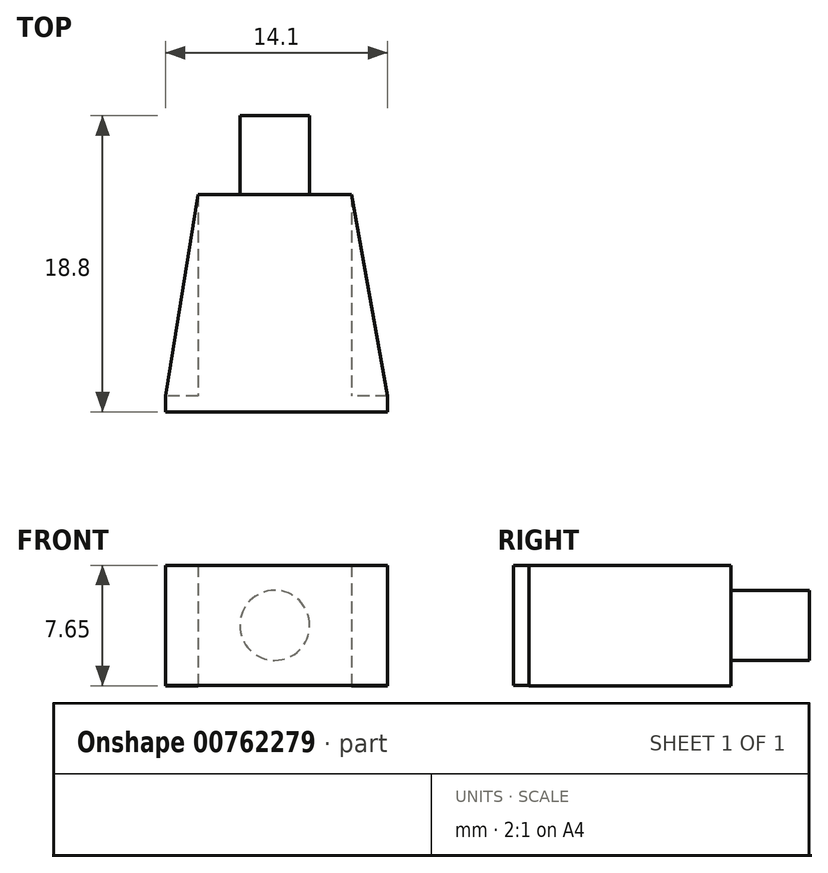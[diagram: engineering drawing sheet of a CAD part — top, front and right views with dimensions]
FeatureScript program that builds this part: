
annotation { "Feature Type Name" : "Feature", "Feature Type Description" : "" }
export const myFeature = defineFeature(function(context is Context, id is Id, definition is map)
    precondition{}
    {
        {
            var Q0;
            Q0=qCreatedBy(makeId("Front.planeOp"),FACE);
            var sketch = newSketch(context, id + "F0", { "sketchPlane" : qUnion([Q0])});
            skLineSegment(sketch, "E0", {"start": v(0, 0) * mm, "end": v(0, 7.63) * mm});
            skLineSegment(sketch, "E1", {"start": v(0, 7.63) * mm, "end": v(14.1, 7.63) * mm});
            skLineSegment(sketch, "E2", {"start": v(14.1, 7.63) * mm, "end": v(14.1, 0) * mm});
            skLineSegment(sketch, "E3", {"start": v(14.1, 0) * mm, "end": v(0, 0) * mm});
            skSolve(sketch);
        }
        {
            var Q0;
            Q0 = qSketchRegion(id + "F0", true);
            extrude(context, id + "F1", {"entities" : qUnion([Q0]), "depth" : 1 * mm, "offsetDistance" : 25.4 * mm});
        }
        {
            var Q0;
            Q0=makeQuery(id+"F1.opExtrude","CAP_FACE",FACE,{"disambiguationData":[OSD([sQuery(id+"F0.wireOp",EDGE,"E0"),sQuery(id+"F0.wireOp",EDGE,"E1"),sQuery(id+"F0.wireOp",EDGE,"E2"),sQuery(id+"F0.wireOp",EDGE,"E3")])],"isStart":true});
            var sketch = newSketch(context, id + "F2", { "sketchPlane" : qUnion([Q0])});
            skLineSegment(sketch, "E4", {"start": v(-11.82, 7.63) * mm, "end": v(-11.82, 0) * mm});
            skLineSegment(sketch, "E5", {"start": v(-2.05, 7.63) * mm, "end": v(-2.05, 0) * mm});
            skLineSegment(sketch, "E6", {"start": v(-11.82, 0) * mm, "end": v(-2.05, 0) * mm});
            skLineSegment(sketch, "E7", {"start": v(-2.05, 7.63) * mm, "end": v(-11.82, 7.63) * mm});
            skSolve(sketch);
        }
        {
            var Q0;
            Q0 = qSketchRegion(id + "F2", true);
            extrude(context, id + "F3", {"entities" : qUnion([Q0]), "operationType" : NewBodyOperationType.ADD, "depth" : 12.8 * mm, "offsetDistance" : 25 * mm});
        }
        {
            var Q0;
            Q0=makeQuery(id+"F3.boolean.opBoolean","MERGE",FACE,{"derivedFrom":[makeQuery(id+"F1.opExtrude","SWEPT_FACE",FACE,{"disambiguationData":[OSD([sQuery(id+"F0.wireOp",EDGE,"E1")])]}),makeQuery(id+"F3.opExtrude","SWEPT_FACE",FACE,{"disambiguationData":[OSD([sQuery(id+"F2.wireOp",EDGE,"E7")])]})]});
            var sketch = newSketch(context, id + "F4", { "sketchPlane" : qUnion([Q0])});
            skLineSegment(sketch, "E8", {"start": v(14.1, 0) * mm, "end": v(11.82, 12.8) * mm});
            skLineSegment(sketch, "E9", {"start": v(11.82, 12.8) * mm, "end": v(11.82, 0) * mm});
            skLineSegment(sketch, "E10", {"start": v(11.82, 0) * mm, "end": v(14.1, 0) * mm});
            skLineSegment(sketch, "E11", {"start": v(2.05, 12.8) * mm, "end": v(0, 0) * mm});
            skLineSegment(sketch, "E12", {"start": v(0, 0) * mm, "end": v(2.05, 0) * mm});
            skLineSegment(sketch, "E13", {"start": v(2.05, 0) * mm, "end": v(2.05, 12.8) * mm});
            skSolve(sketch);
        }
        {
            var Q0;
            Q0 = qSketchRegion(id + "F4", true);
            extrude(context, id + "F5", {"entities" : qUnion([Q0]), "operationType" : NewBodyOperationType.ADD, "oppositeDirection" : true, "depth" : 7.65 * mm, "offsetDistance" : 25 * mm});
        }
        {
            var Q0;
            Q0=makeQuery(id+"F3.opExtrude","CAP_FACE",FACE,{"disambiguationData":[OSD([sQuery(id+"F2.wireOp",EDGE,"E4"),sQuery(id+"F2.wireOp",EDGE,"E5"),sQuery(id+"F2.wireOp",EDGE,"E6"),sQuery(id+"F2.wireOp",EDGE,"E7")])],"isStart":false});
            var sketch = newSketch(context, id + "F6", { "sketchPlane" : qUnion([Q0])});
            skCircle(sketch, "E14", {"center": v(-6.94, 3.81) * mm, "radius": 2.22 * mm});
            skPoint(sketch, "E14.centerSnap0", {"position": v(-6.94, 0) * mm});
            skPoint(sketch, "E14.centerSnap1", {"position": v(-2.05, 3.81) * mm});
            skSolve(sketch);
        }
        {
            var Q0;
            Q0 = qSketchRegion(id + "F6", true);
            extrude(context, id + "F7", {"entities" : qUnion([Q0]), "operationType" : NewBodyOperationType.ADD, "depth" : 5 * mm, "offsetDistance" : 25 * mm});
        }
    });
